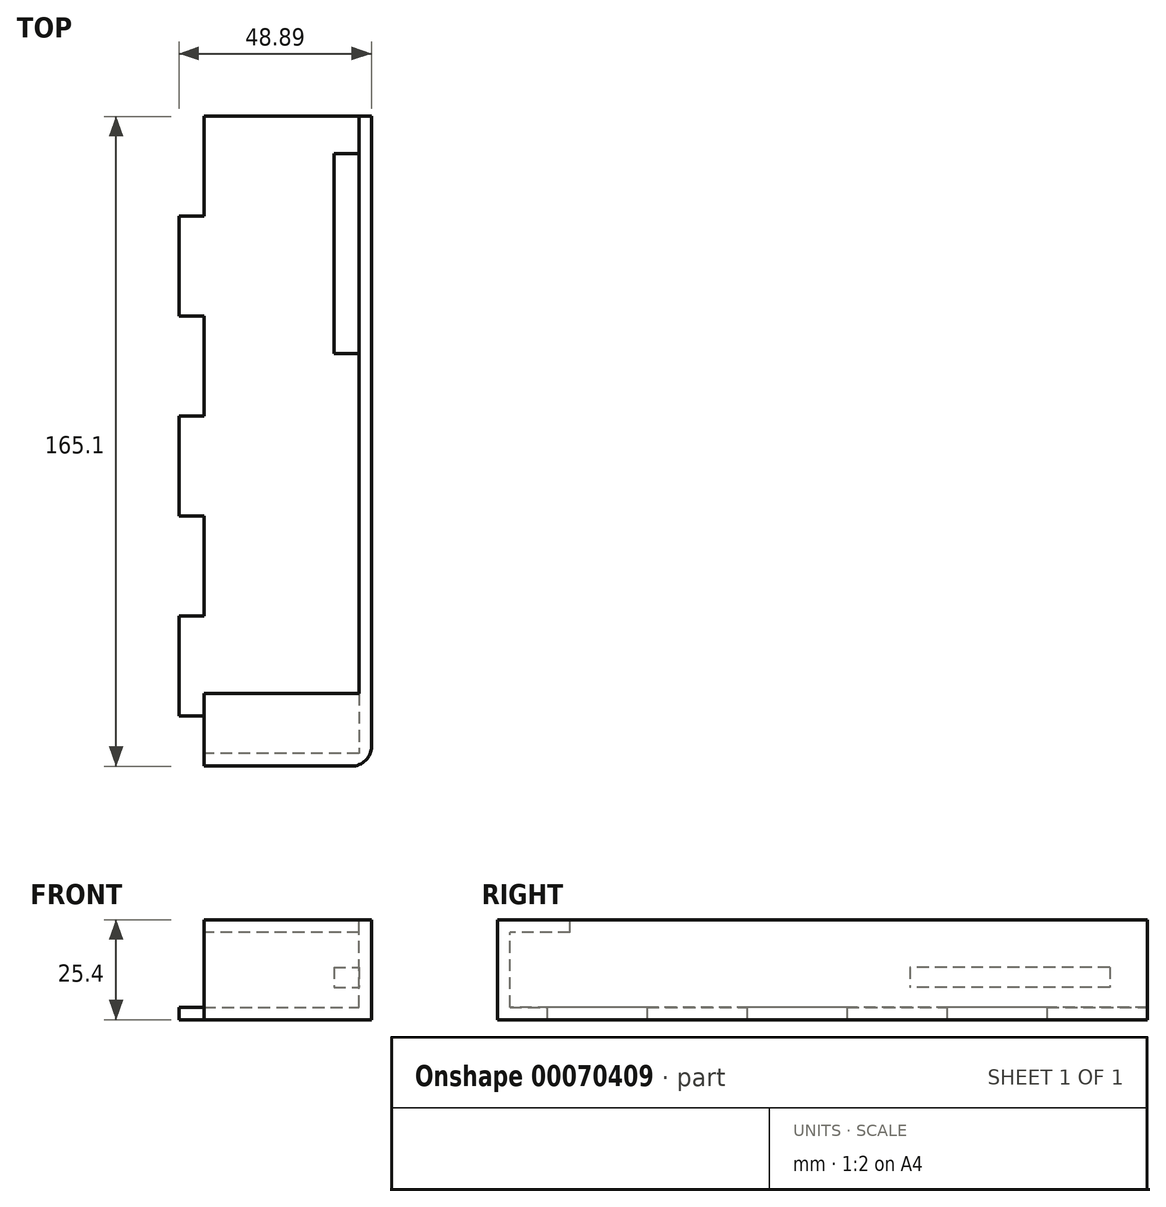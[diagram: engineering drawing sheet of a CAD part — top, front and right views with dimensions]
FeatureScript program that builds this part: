
annotation { "Feature Type Name" : "Feature", "Feature Type Description" : "" }
export const myFeature = defineFeature(function(context is Context, id is Id, definition is map)
    precondition{}
    {
        {
            var Q0;
            Q0=qCreatedBy(makeId("Top.planeOp"),FACE);
            var sketch = newSketch(context, id + "F0", { "sketchPlane" : qUnion([Q0])});
            skLineSegment(sketch, "E0", {"start": v(-45.53, 120.71) * mm, "end": v(39.56, 120.71) * mm});
            skLineSegment(sketch, "E1", {"start": v(39.56, -44.39) * mm, "end": v(-45.53, -44.39) * mm});
            skLineSegment(sketch, "E2.0", {"start": v(-45.53, 120.71) * mm, "end": v(-45.53, -44.39) * mm});
            skLineSegment(sketch, "E3.0", {"start": v(39.56, 120.71) * mm, "end": v(39.56, -44.39) * mm});
            skSolve(sketch);
        }
        {
            var Q0;
            Q0 = qSketchRegion(id + "F0", true);
            extrude(context, id + "F1", {"entities" : qUnion([Q0]), "depth" : 25.4 * mm});
        }
        {
            var Q0;
            Q0=makeQuery(id+"F1.opExtrude","CAP_FACE",FACE,{"disambiguationData":[OSD([sQuery(id+"F0.wireOp",EDGE,"13c80bd3-2ed5-4597-9aef-5bcd11f7814c.left"),sQuery(id+"F0.wireOp",EDGE,"13c80bd3-2ed5-4597-9aef-5bcd11f7814c.right"),sQuery(id+"F0.wireOp",EDGE,"E0"),sQuery(id+"F0.wireOp",EDGE,"E1")])],"isStart":false});
            var sketch = newSketch(context, id + "F2", { "sketchPlane" : qUnion([Q0])});
            skLineSegment(sketch, "E4.0", {"start": v(36.39, 120.71) * mm, "end": v(36.39, -41.21) * mm});
            skLineSegment(sketch, "E4.1", {"start": v(36.39, -41.21) * mm, "end": v(-2.98, -41.21) * mm});
            skLineSegment(sketch, "E5", {"start": v(-2.98, -44.39) * mm, "end": v(-2.98, -41.21) * mm});
            skPoint(sketch, "E4.2.end.orphan", {"position": v(-42.35, -41.21) * mm});
            skLineSegment(sketch, "E6", {"start": v(-2.98, -41.21) * mm, "end": v(-2.98, 120.71) * mm});
            skSolve(sketch);
        }
        {
            var Q0;
            {var subQ0=sQuery(id+"F2.wireOp",EDGE,"E4.0");Q0=makeQuery(id+"F2.imprint","IMPRINT",FACE,{"disambiguationData":[TD([[makeQuery(id+"F2.imprint","IMPRINT",EDGE,{"derivedFrom":subQ0}),-1.0]])]});}
            extrude(context, id + "F3", {"entities" : qUnion([Q0]), "operationType" : NewBodyOperationType.REMOVE, "oppositeDirection" : true, "depth" : 22.22 * mm});
        }
        {
            var Q0;
            Q0=makeQuery(id+"F3.boolean.opBoolean","COPY",FACE,{"derivedFrom":makeQuery(id+"F3.opExtrude","SWEPT_FACE",FACE,{"disambiguationData":[OSD([sQuery(id+"F2.wireOp",EDGE,"E4.0")])]})});
            var sketch = newSketch(context, id + "F4", { "sketchPlane" : qUnion([Q0])});
            skLineSegment(sketch, "E7.bottom", {"start": v(-111.19, 13.34) * mm, "end": v(-60.39, 13.34) * mm});
            skLineSegment(sketch, "E7.top", {"start": v(-111.19, 8.25) * mm, "end": v(-60.39, 8.26) * mm});
            skLineSegment(sketch, "E7.left", {"start": v(-111.19, 13.33) * mm, "end": v(-111.19, 8.25) * mm});
            skLineSegment(sketch, "E7.right", {"start": v(-60.39, 13.33) * mm, "end": v(-60.39, 8.26) * mm});
            skSolve(sketch);
        }
        {
            var Q0;
            Q0=makeQuery(id+"F4.imprint","IMPRINT",FACE,{"disambiguationData":[TD([[makeQuery(id+"F4.imprint","IMPRINT",EDGE,{"derivedFrom":sQuery(id+"F4.wireOp",EDGE,"E7.bottom")}),-1.0]])]});
            extrude(context, id + "F5", {"entities" : qUnion([Q0]), "operationType" : NewBodyOperationType.ADD, "depth" : 6.35 * mm});
        }
        {
            var Q0;
            Q0=makeQuery(id+"F1.opExtrude","CAP_FACE",FACE,{"disambiguationData":[OSD([sQuery(id+"F0.wireOp",EDGE,"E0"),sQuery(id+"F0.wireOp",EDGE,"E1"),sQuery(id+"F0.wireOp",EDGE,"E2.0"),sQuery(id+"F0.wireOp",EDGE,"E3.0")])],"isStart":false});
            var sketch = newSketch(context, id + "F6", { "sketchPlane" : qUnion([Q0])});
            skLineSegment(sketch, "E8.bottom", {"start": v(-2.98, 120.71) * mm, "end": v(-45.53, 120.71) * mm});
            skLineSegment(sketch, "E8.top", {"start": v(-2.98, -44.39) * mm, "end": v(-45.53, -44.39) * mm});
            skLineSegment(sketch, "E8.left", {"start": v(-2.98, 120.71) * mm, "end": v(-2.98, -44.39) * mm});
            skLineSegment(sketch, "E8.right", {"start": v(-45.53, 120.71) * mm, "end": v(-45.53, -44.39) * mm});
            skSolve(sketch);
        }
        {
            var Q0;
            {var subQ3=sQuery(id+"F6.wireOp",EDGE,"E8.bottom");Q0=makeQuery(id+"F6.imprint","IMPRINT",FACE,{"disambiguationData":[TD([[makeQuery(id+"F6.imprint","IMPRINT",EDGE,{"derivedFrom":subQ3}),-1.0]])]});}
            extrude(context, id + "F7", {"entities" : qUnion([Q0]), "operationType" : NewBodyOperationType.REMOVE, "endBound" : BoundingType.THROUGH_ALL, "oppositeDirection" : true, "depth" : 25.4 * mm});
        }
        {
            var Q0;
            Q0=makeQuery(id+"F1.opExtrude","CAP_FACE",FACE,{"disambiguationData":[OSD([sQuery(id+"F0.wireOp",EDGE,"E0"),sQuery(id+"F0.wireOp",EDGE,"E1"),sQuery(id+"F0.wireOp",EDGE,"E2.0"),sQuery(id+"F0.wireOp",EDGE,"E3.0")])],"isStart":false});
            var sketch = newSketch(context, id + "F8", { "sketchPlane" : qUnion([Q0])});
            skLineSegment(sketch, "E9.bottom", {"start": v(-2.98, -41.21) * mm, "end": v(36.39, -41.21) * mm});
            skLineSegment(sketch, "E9.top", {"start": v(-2.98, -25.97) * mm, "end": v(36.39, -25.97) * mm});
            skLineSegment(sketch, "E9.left", {"start": v(-2.98, -41.21) * mm, "end": v(-2.98, -25.97) * mm});
            skLineSegment(sketch, "E9.right", {"start": v(36.39, -41.21) * mm, "end": v(36.39, -25.97) * mm});
            skSolve(sketch);
        }
        {
            var Q0;
            Q0=makeQuery(id+"F8.imprint","IMPRINT",FACE,{"disambiguationData":[TD([[makeQuery(id+"F8.imprint","IMPRINT",EDGE,{"derivedFrom":sQuery(id+"F8.wireOp",EDGE,"E9.bottom")}),-1.0]])]});
            extrude(context, id + "F9", {"entities" : qUnion([Q0]), "operationType" : NewBodyOperationType.ADD, "oppositeDirection" : true, "depth" : 3.17 * mm});
        }
        {
            var Q0;
            Q0=makeQuery(id+"F3.boolean.opBoolean","COPY",FACE,{"derivedFrom":makeQuery(id+"F3.opExtrude","CAP_FACE",FACE,{"disambiguationData":[OSD([sQuery(id+"F0.wireOp",EDGE,"E0"),sQuery(id+"F2.wireOp",EDGE,"E4.0"),sQuery(id+"F2.wireOp",EDGE,"E4.1"),sQuery(id+"F2.wireOp",EDGE,"E6")])],"isStart":false})});
            var sketch = newSketch(context, id + "F10", { "sketchPlane" : qUnion([Q0])});
            skLineSegment(sketch, "E10.bottom", {"start": v(-2.98, 95.31) * mm, "end": v(-9.33, 95.31) * mm});
            skLineSegment(sketch, "E10.top", {"start": v(-2.98, 69.91) * mm, "end": v(-9.33, 69.91) * mm});
            skLineSegment(sketch, "E10.left", {"start": v(-2.98, 95.31) * mm, "end": v(-2.98, 69.91) * mm});
            skLineSegment(sketch, "E10.right", {"start": v(-9.33, 95.31) * mm, "end": v(-9.33, 69.91) * mm});
            skLineSegment(sketch, "E11.0.1.0", {"start": v(-9.33, 44.51) * mm, "end": v(-9.33, 19.11) * mm});
            skLineSegment(sketch, "E11.0.1.1", {"start": v(-2.98, 19.11) * mm, "end": v(-9.33, 19.11) * mm});
            skLineSegment(sketch, "E11.0.1.2", {"start": v(-2.98, 44.51) * mm, "end": v(-2.98, 19.11) * mm});
            skLineSegment(sketch, "E11.0.1.3", {"start": v(-2.98, 44.51) * mm, "end": v(-9.33, 44.51) * mm});
            skLineSegment(sketch, "E11.0.2.0", {"start": v(-9.33, -6.29) * mm, "end": v(-9.33, -31.69) * mm});
            skLineSegment(sketch, "E11.0.2.1", {"start": v(-2.98, -31.69) * mm, "end": v(-9.33, -31.69) * mm});
            skLineSegment(sketch, "E11.0.2.2", {"start": v(-2.98, -6.29) * mm, "end": v(-2.98, -31.69) * mm});
            skLineSegment(sketch, "E11.0.2.3", {"start": v(-2.98, -6.29) * mm, "end": v(-9.33, -6.29) * mm});
            skLineSegment(sketch, "E11.direction1", {"start": v(-9.33, 69.91) * mm, "end": v(19.24, 69.91) * mm, "construction": true});
            skLineSegment(sketch, "E11.direction2", {"start": v(-9.33, 69.91) * mm, "end": v(-9.33, 19.11) * mm, "construction": true});
            skSolve(sketch);
        }
        {
            var Q0;
            Q0=makeQuery(id+"F10.imprint","IMPRINT",FACE,{"disambiguationData":[TD([[makeQuery(id+"F10.imprint","IMPRINT",EDGE,{"derivedFrom":sQuery(id+"F10.wireOp",EDGE,"E10.bottom")}),1.0]])]});
            var Q1;
            Q1=makeQuery(id+"F10.imprint","IMPRINT",FACE,{"disambiguationData":[TD([[makeQuery(id+"F10.imprint","IMPRINT",EDGE,{"derivedFrom":sQuery(id+"F10.wireOp",EDGE,"E11.0.1.0")}),1.0]])]});
            var Q2;
            Q2=makeQuery(id+"F10.imprint","IMPRINT",FACE,{"disambiguationData":[TD([[makeQuery(id+"F10.imprint","IMPRINT",EDGE,{"derivedFrom":sQuery(id+"F10.wireOp",EDGE,"E11.0.2.0")}),1.0]])]});
            extrude(context, id + "F11", {"entities" : qUnion([Q0, Q1, Q2]), "operationType" : NewBodyOperationType.ADD, "oppositeDirection" : true, "depth" : 3.17 * mm});
        }
        {
            var Q0;
            Q0=makeQuery(id+"F1.opExtrude","SWEPT_EDGE",EDGE,{"disambiguationData":[OSD([sQuery(id+"F0.wireOp",EDGE,"E1"),sQuery(id+"F0.wireOp",EDGE,"E3.0")])]});
            fillet(context, id + "F12", {"entities" : qUnion([Q0]), "radius" : 5.08 * mm, "tangentPropagation" : true, "allowEdgeOverflow" : false});
        }
    });
